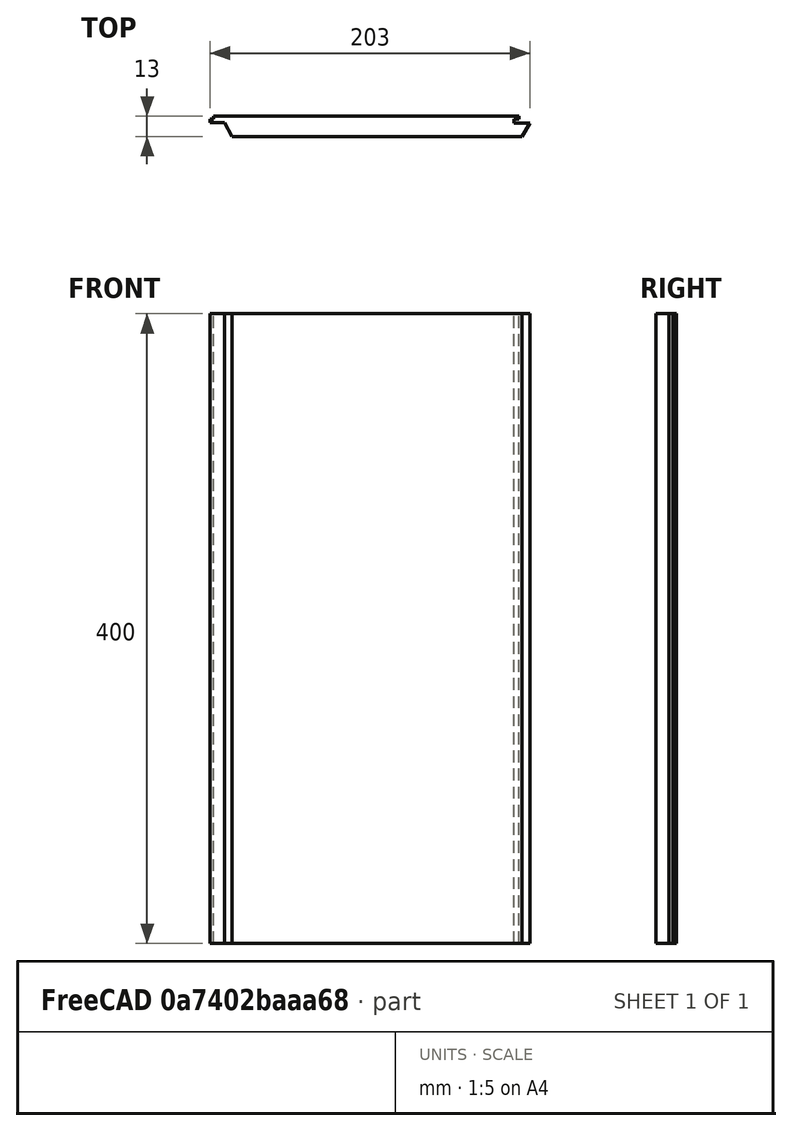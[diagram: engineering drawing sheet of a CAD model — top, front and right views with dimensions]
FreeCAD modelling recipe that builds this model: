
FCSTD DOCUMENT  (FreeCAD 0.19R24276 (Git))
Label: Parket_L400
License: All rights reserved
LicenseURL: http://en.wikipedia.org/wiki/All_rights_reserved
objects: PartDesign::Body×2, Sketcher::SketchObject×1, PartDesign::Pad×1
note: 5 computed .brp shape members not serialized (recipe doc carries the construction recipe); baked Part::Feature solids carry a one-line shape summary decoded from their .brp

FEATURE [Sketcher::SketchObject] Sketch
  FullyConstrained = true
  MapMode = 5
  Support = -> [XY_Plane]
  sketch-geometry (14):
    g0: LineSegment StartX=0 StartY=0 StartZ=0 EndX=184 EndY=0 EndZ=0
    g1: LineSegment StartX=184 StartY=0 StartZ=0 EndX=184 EndY=8.5 EndZ=0
    g2: LineSegment StartX=184 StartY=0 StartZ=0 EndX=189 EndY=8.5 EndZ=0
    g3: LineSegment StartX=184 StartY=8.5 StartZ=0 EndX=179 EndY=8.5 EndZ=0
    g4: LineSegment StartX=179 StartY=8.5 StartZ=0 EndX=179 EndY=11 EndZ=0
    g5: LineSegment StartX=179 StartY=11 StartZ=0 EndX=182 EndY=11 EndZ=0
    g6: LineSegment StartX=182 StartY=11 StartZ=0 EndX=182 EndY=13 EndZ=0
    g7: LineSegment StartX=182 StartY=13 StartZ=0 EndX=-12 EndY=13 EndZ=0
    g8: LineSegment StartX=184 StartY=8.5 StartZ=0 EndX=189 EndY=8.5 EndZ=0
    g9: LineSegment StartX=-12 StartY=13 StartZ=0 EndX=-12 EndY=11 EndZ=0
    g10: LineSegment StartX=-12 StartY=11 StartZ=0 EndX=-14 EndY=11 EndZ=0
    g11: LineSegment StartX=-14 StartY=11 StartZ=0 EndX=-14 EndY=9 EndZ=0
    g12: LineSegment StartX=-14 StartY=9 StartZ=0 EndX=-5 EndY=9 EndZ=0
    g13: LineSegment StartX=-5 StartY=9 StartZ=0 EndX=0 EndY=0 EndZ=0
  constraints (40):
    c: Coincident(g0,g-1)
    c: PointOnObject(g0,g-1)
    c: DistanceX(g0,g0) = 184
    c: Coincident(g1,g0)
    c: Vertical(g1)
    c: DistanceY(g1,g1) = 8.5
    c: Coincident(g2,g0)
    c: Coincident(g3,g1)
    c: DistanceX(g3,g3) = 5
    c: Horizontal(g3)
    c: Coincident(g4,g3)
    c: Vertical(g4)
    c: DistanceY(g4,g4) = 2.5
    c: Coincident(g5,g4)
    c: Horizontal(g5)
    c: DistanceX(g5,g5) = 3
    c: Coincident(g6,g5)
    c: Vertical(g6)
    c: Coincident(g7,g6)
    c: Horizontal(g7)
    c: Coincident(g8,g1)
    c: Horizontal(g8)
    c: Coincident(g2,g8)
    c: DistanceX(g7,g7) = 194
    c: Coincident(g9,g7)
    c: Vertical(g9)
    c: Coincident(g10,g9)
    c: Coincident(g11,g10)
    c: Coincident(g12,g11)
    c: Horizontal(g12)
    c: Coincident(g13,g12)
    c: Coincident(g13,g-1)
    c: DistanceX(g10,g10) = 2
    c: Vertical(g11)
    c: DistanceY(g9,g9) = 2
    c: Horizontal(g10)
    c: DistanceY(g11,g11) = 2
    c: DistanceY(g6,g6) = 2
    c: DistanceX(g12,g-1) = 5
    c: DistanceX(g0,g2) = 5
FEATURE [PartDesign::Pad] Pad
  Direction = (1,1,1)
  Length = 400
  Length2 = 100
  Profile = -> Sketch
  Type = 0
FEATURE [PartDesign::Body] Body
  Group = -> [Sketch,Pad]
  Origin = -> Origin
  Tip = -> Pad
FEATURE [PartDesign::Body] Body001
  Origin = -> Origin001
